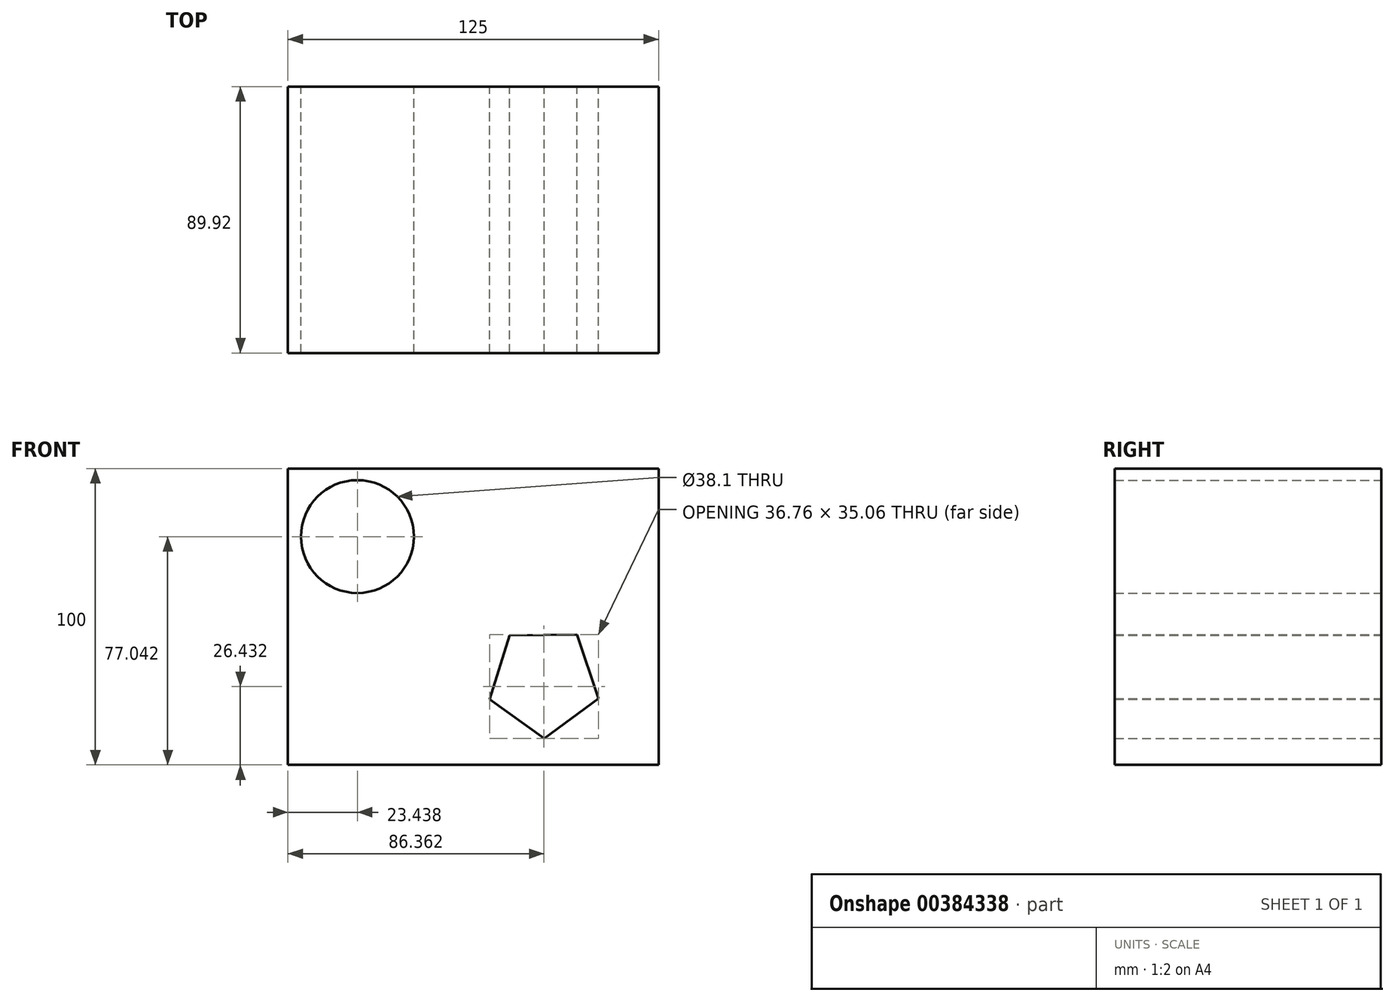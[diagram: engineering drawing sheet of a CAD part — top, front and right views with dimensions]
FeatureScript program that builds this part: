
annotation { "Feature Type Name" : "Feature", "Feature Type Description" : "" }
export const myFeature = defineFeature(function(context is Context, id is Id, definition is map)
    precondition{}
    {
        {
            var Q0;
            Q0=qCreatedBy(makeId("Front.planeOp"),FACE);
            var sketch = newSketch(context, id + "F0", { "sketchPlane" : qUnion([Q0])});
            skLineSegment(sketch, "E0.bottom", {"start": v(62.5, -50) * mm, "end": v(-62.5, -50) * mm});
            skLineSegment(sketch, "E0.top", {"start": v(62.5, 50) * mm, "end": v(-62.5, 50) * mm});
            skLineSegment(sketch, "E0.left", {"start": v(62.5, -50) * mm, "end": v(62.5, 50) * mm});
            skLineSegment(sketch, "E0.right", {"start": v(-62.5, -50) * mm, "end": v(-62.5, 50) * mm});
            skPoint(sketch, "E0.middle", {"position": v(0, 0) * mm});
            skCircle(sketch, "E1", {"center": v(-39.06, 27.04) * mm, "radius": 19.05 * mm});
            skCircle(sketch, "E2.cCircle", {"center": v(23.8, -21.77) * mm, "radius": 15.64 * mm, "construction": true});
            skLineSegment(sketch, "E2.0", {"start": v(42.24, -27.58) * mm, "end": v(23.98, -41.1) * mm});
            skLineSegment(sketch, "E2.1", {"start": v(23.98, -41.1) * mm, "end": v(5.48, -27.9) * mm});
            skLineSegment(sketch, "E2.2", {"start": v(5.48, -27.9) * mm, "end": v(12.31, -6.24) * mm});
            skLineSegment(sketch, "E2.3", {"start": v(12.31, -6.24) * mm, "end": v(35.03, -6.04) * mm});
            skLineSegment(sketch, "E2.4", {"start": v(35.03, -6.04) * mm, "end": v(42.24, -27.58) * mm});
            skPoint(sketch, "E2.0.midPoint", {"position": v(33.11, -34.34) * mm});
            skSolve(sketch);
        }
        {
            var Q0;
            Q0 = qSketchRegion(id + "F0", true);
            extrude(context, id + "F1", {"entities" : qUnion([Q0]), "depth" : 89.92 * mm});
        }
    });
